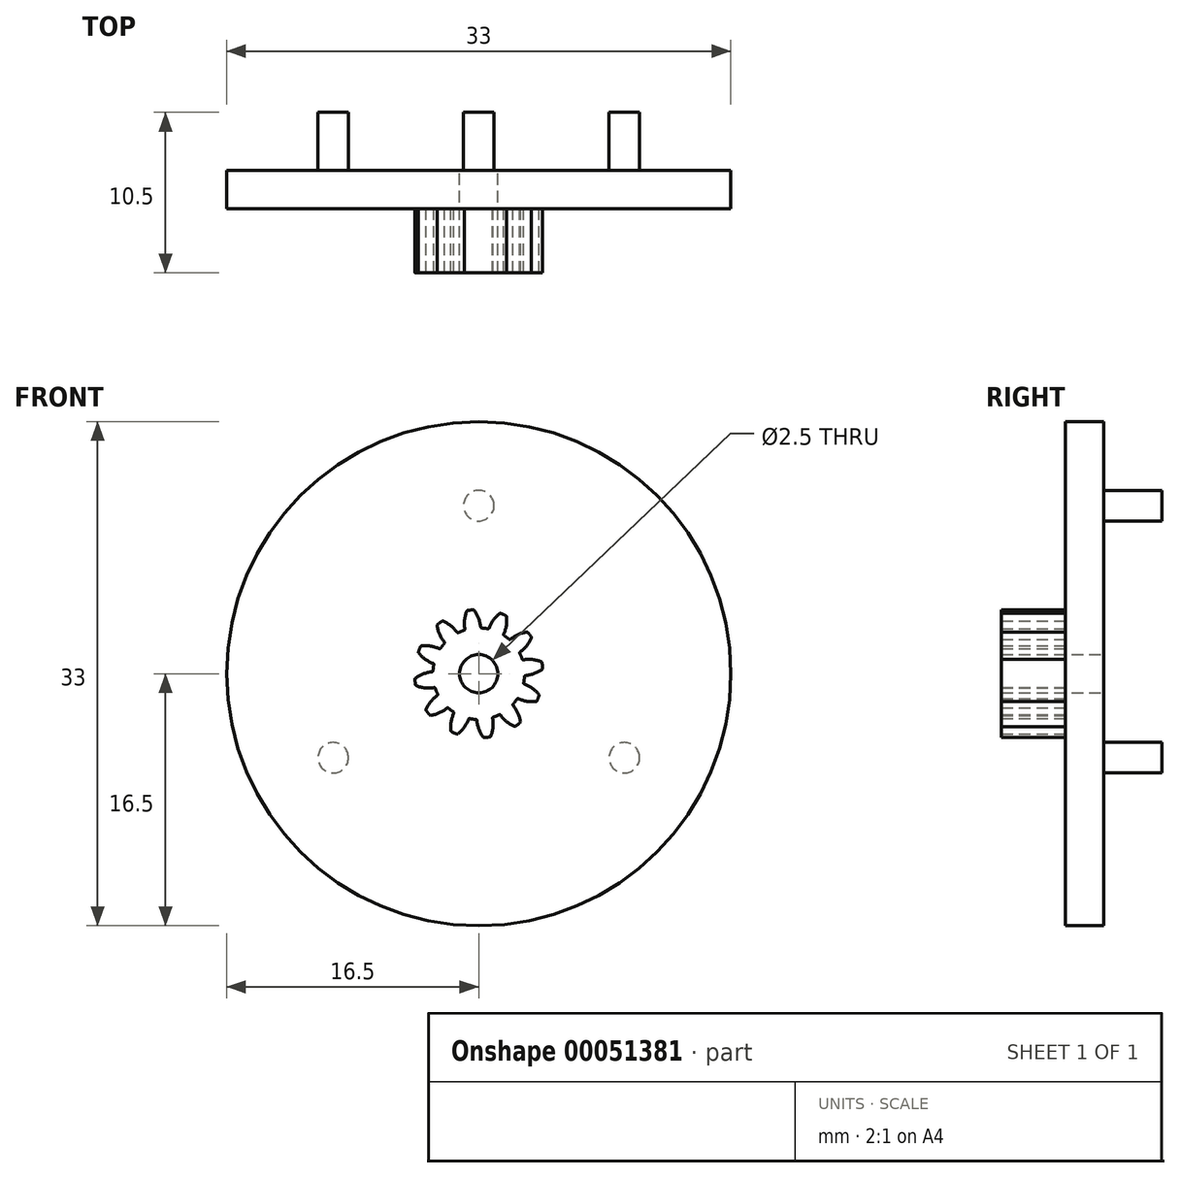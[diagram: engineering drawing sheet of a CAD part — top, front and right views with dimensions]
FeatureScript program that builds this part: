
annotation { "Feature Type Name" : "Feature", "Feature Type Description" : "" }
export const myFeature = defineFeature(function(context is Context, id is Id, definition is map)
    precondition{}
    {
        {
            var Q0;
            Q0=qCreatedBy(makeId("Front.planeOp"),FACE);
            var sketch = newSketch(context, id + "F0", { "sketchPlane" : qUnion([Q0])});
            skCircle(sketch, "E0", {"center": v(0, 0) * mm, "radius": 4.2 * mm, "construction": true});
            skCircle(sketch, "E1", {"center": v(0, 0) * mm, "radius": 3.6 * mm, "construction": true});
            skCircle(sketch, "E2", {"center": v(0, 0) * mm, "radius": 3 * mm, "construction": true});
            skLineSegment(sketch, "E3", {"start": v(0, 0) * mm, "end": v(0, 0.84) * mm, "construction": true});
            skLineSegment(sketch, "E4", {"start": v(0, 3.6) * mm, "end": v(-6.08, 3.6) * mm, "construction": true});
            skLineSegment(sketch, "E5", {"start": v(0, 3.6) * mm, "end": v(-6.1, 1.38) * mm, "construction": true});
            skCircle(sketch, "E6", {"center": v(0, 3.6) * mm, "radius": 2.16 * mm, "construction": true});
            skCircle(sketch, "E7", {"center": v(-2.03, 2.86) * mm, "radius": 2.16 * mm, "construction": true});
            skArc(sketch, "E8", {"start": v(-0.3, 4.16) * mm, "mid": v(-0.01, 3.64) * mm, "end": v(0.12, 3.06) * mm});
            skPoint(sketch, "E9.0.midPoint", {"position": v(-1.28, 0.84) * mm});
            skCircle(sketch, "E10.cCircle", {"center": v(0, 0) * mm, "radius": 0.84 * mm, "construction": true});
            skLineSegment(sketch, "E10.0", {"start": v(0, 0.84) * mm, "end": v(0.1, 0.83) * mm, "construction": true});
            skLineSegment(sketch, "E10.1", {"start": v(0.1, 0.83) * mm, "end": v(0.22, 0.8) * mm, "construction": true});
            skLineSegment(sketch, "E10.2", {"start": v(0.22, 0.8) * mm, "end": v(0.32, 0.77) * mm, "construction": true});
            skLineSegment(sketch, "E10.3", {"start": v(0.32, 0.77) * mm, "end": v(0.42, 0.72) * mm, "construction": true});
            skLineSegment(sketch, "E10.4", {"start": v(0.42, 0.72) * mm, "end": v(0.5, 0.66) * mm, "construction": true});
            skLineSegment(sketch, "E10.5", {"start": v(0.5, 0.66) * mm, "end": v(0.6, 0.6) * mm, "construction": true});
            skLineSegment(sketch, "E10.6", {"start": v(0.6, 0.6) * mm, "end": v(0.66, 0.5) * mm, "construction": true});
            skLineSegment(sketch, "E10.7", {"start": v(0.66, 0.5) * mm, "end": v(0.72, 0.42) * mm, "construction": true});
            skLineSegment(sketch, "E10.8", {"start": v(0.72, 0.42) * mm, "end": v(0.77, 0.32) * mm, "construction": true});
            skLineSegment(sketch, "E10.9", {"start": v(0.77, 0.32) * mm, "end": v(0.8, 0.22) * mm, "construction": true});
            skLineSegment(sketch, "E10.10", {"start": v(0.8, 0.22) * mm, "end": v(0.83, 0.1) * mm, "construction": true});
            skLineSegment(sketch, "E10.11", {"start": v(0.83, 0.1) * mm, "end": v(0.84, 0) * mm, "construction": true});
            skLineSegment(sketch, "E10.12", {"start": v(0.84, 0) * mm, "end": v(0.83, -0.1) * mm, "construction": true});
            skLineSegment(sketch, "E10.13", {"start": v(0.83, -0.1) * mm, "end": v(0.8, -0.22) * mm, "construction": true});
            skLineSegment(sketch, "E10.14", {"start": v(0.8, -0.22) * mm, "end": v(0.77, -0.32) * mm, "construction": true});
            skLineSegment(sketch, "E10.15", {"start": v(0.77, -0.32) * mm, "end": v(0.72, -0.42) * mm, "construction": true});
            skLineSegment(sketch, "E10.16", {"start": v(0.72, -0.42) * mm, "end": v(0.66, -0.5) * mm, "construction": true});
            skLineSegment(sketch, "E10.17", {"start": v(0.66, -0.5) * mm, "end": v(0.6, -0.6) * mm, "construction": true});
            skLineSegment(sketch, "E10.18", {"start": v(0.6, -0.6) * mm, "end": v(0.5, -0.66) * mm, "construction": true});
            skLineSegment(sketch, "E10.19", {"start": v(0.5, -0.66) * mm, "end": v(0.42, -0.72) * mm, "construction": true});
            skLineSegment(sketch, "E10.20", {"start": v(0.42, -0.72) * mm, "end": v(0.32, -0.77) * mm, "construction": true});
            skLineSegment(sketch, "E10.21", {"start": v(0.32, -0.77) * mm, "end": v(0.22, -0.8) * mm, "construction": true});
            skLineSegment(sketch, "E10.22", {"start": v(0.22, -0.8) * mm, "end": v(0.1, -0.83) * mm, "construction": true});
            skLineSegment(sketch, "E10.23", {"start": v(0.1, -0.83) * mm, "end": v(0, -0.84) * mm, "construction": true});
            skLineSegment(sketch, "E10.24", {"start": v(0, -0.84) * mm, "end": v(-0.1, -0.83) * mm, "construction": true});
            skLineSegment(sketch, "E10.25", {"start": v(-0.1, -0.83) * mm, "end": v(-0.22, -0.8) * mm, "construction": true});
            skLineSegment(sketch, "E10.26", {"start": v(-0.22, -0.8) * mm, "end": v(-0.32, -0.77) * mm, "construction": true});
            skLineSegment(sketch, "E10.27", {"start": v(-0.32, -0.77) * mm, "end": v(-0.42, -0.72) * mm, "construction": true});
            skLineSegment(sketch, "E10.28", {"start": v(-0.42, -0.72) * mm, "end": v(-0.5, -0.66) * mm, "construction": true});
            skLineSegment(sketch, "E10.29", {"start": v(-0.5, -0.66) * mm, "end": v(-0.6, -0.6) * mm, "construction": true});
            skLineSegment(sketch, "E10.30", {"start": v(-0.6, -0.6) * mm, "end": v(-0.66, -0.5) * mm, "construction": true});
            skLineSegment(sketch, "E10.31", {"start": v(-0.66, -0.5) * mm, "end": v(-0.72, -0.42) * mm, "construction": true});
            skLineSegment(sketch, "E10.32", {"start": v(-0.72, -0.42) * mm, "end": v(-0.77, -0.32) * mm, "construction": true});
            skLineSegment(sketch, "E10.33", {"start": v(-0.77, -0.32) * mm, "end": v(-0.8, -0.22) * mm, "construction": true});
            skLineSegment(sketch, "E10.34", {"start": v(-0.8, -0.22) * mm, "end": v(-0.83, -0.1) * mm, "construction": true});
            skLineSegment(sketch, "E10.35", {"start": v(-0.83, -0.1) * mm, "end": v(-0.84, 0) * mm, "construction": true});
            skLineSegment(sketch, "E10.36", {"start": v(-0.84, 0) * mm, "end": v(-0.83, 0.1) * mm, "construction": true});
            skLineSegment(sketch, "E10.37", {"start": v(-0.83, 0.1) * mm, "end": v(-0.8, 0.22) * mm, "construction": true});
            skLineSegment(sketch, "E10.38", {"start": v(-0.8, 0.22) * mm, "end": v(-0.77, 0.32) * mm, "construction": true});
            skLineSegment(sketch, "E10.39", {"start": v(-0.77, 0.32) * mm, "end": v(-0.72, 0.42) * mm, "construction": true});
            skLineSegment(sketch, "E10.40", {"start": v(-0.72, 0.42) * mm, "end": v(-0.66, 0.5) * mm, "construction": true});
            skLineSegment(sketch, "E10.41", {"start": v(-0.66, 0.5) * mm, "end": v(-0.6, 0.6) * mm, "construction": true});
            skLineSegment(sketch, "E10.42", {"start": v(-0.6, 0.6) * mm, "end": v(-0.5, 0.66) * mm, "construction": true});
            skLineSegment(sketch, "E10.43", {"start": v(-0.5, 0.66) * mm, "end": v(-0.42, 0.72) * mm, "construction": true});
            skLineSegment(sketch, "E10.44", {"start": v(-0.42, 0.72) * mm, "end": v(-0.32, 0.77) * mm, "construction": true});
            skLineSegment(sketch, "E10.45", {"start": v(-0.32, 0.77) * mm, "end": v(-0.22, 0.8) * mm, "construction": true});
            skLineSegment(sketch, "E10.46", {"start": v(-0.22, 0.8) * mm, "end": v(-0.1, 0.83) * mm, "construction": true});
            skLineSegment(sketch, "E10.47", {"start": v(-0.1, 0.83) * mm, "end": v(0, 0.84) * mm, "construction": true});
            skLineSegment(sketch, "E11", {"start": v(0, 0) * mm, "end": v(-0.1, 0.83) * mm, "construction": true});
            skArc(sketch, "E12.MirrorCS", {"start": v(-0.79, 4.1) * mm, "mid": v(-0.93, 3.52) * mm, "end": v(-0.9, 2.92) * mm});
            skArc(sketch, "E13", {"start": v(-0.73, 4.14) * mm, "mid": v(-0.55, 4.16) * mm, "end": v(-0.36, 4.18) * mm});
            skArc(sketch, "E14", {"start": v(-0.96, 2.84) * mm, "mid": v(0.4, -2.97) * mm, "end": v(0.19, 3) * mm});
            skPoint(sketch, "E15.visualSharp", {"position": v(-0.9, 2.86) * mm});
            skArc(sketch, "E15.filletArc", {"start": v(-0.96, 2.84) * mm, "mid": v(-0.92, 2.87) * mm, "end": v(-0.9, 2.92) * mm});
            skPoint(sketch, "E16.visualSharp", {"position": v(-0.77, 4.13) * mm});
            skArc(sketch, "E16.filletArc", {"start": v(-0.73, 4.14) * mm, "mid": v(-0.76, 4.12) * mm, "end": v(-0.79, 4.1) * mm});
            skPoint(sketch, "E17.visualSharp", {"position": v(-0.32, 4.19) * mm});
            skArc(sketch, "E17.filletArc", {"start": v(-0.3, 4.16) * mm, "mid": v(-0.33, 4.18) * mm, "end": v(-0.36, 4.18) * mm});
            skArc(sketch, "E18.filletArc", {"start": v(0.12, 3.06) * mm, "mid": v(0.14, 3.01) * mm, "end": v(0.19, 3) * mm});
            skArc(sketch, "E19.1.0", {"start": v(-2.25, 1.98) * mm, "mid": v(-2.23, 2.03) * mm, "end": v(-2.25, 2.08) * mm});
            skArc(sketch, "E19.1.1", {"start": v(-2.73, 3.15) * mm, "mid": v(-2.56, 2.58) * mm, "end": v(-2.25, 2.08) * mm});
            skArc(sketch, "E19.1.2", {"start": v(-2.7, 3.22) * mm, "mid": v(-2.72, 3.19) * mm, "end": v(-2.73, 3.15) * mm});
            skArc(sketch, "E19.1.3", {"start": v(-2.7, 3.22) * mm, "mid": v(-2.56, 3.33) * mm, "end": v(-2.4, 3.44) * mm});
            skArc(sketch, "E19.1.4", {"start": v(-2.34, 3.45) * mm, "mid": v(-2.37, 3.45) * mm, "end": v(-2.4, 3.44) * mm});
            skArc(sketch, "E19.1.5", {"start": v(-2.34, 3.45) * mm, "mid": v(-1.83, 3.14) * mm, "end": v(-1.42, 2.71) * mm});
            skArc(sketch, "E19.1.6", {"start": v(-1.42, 2.71) * mm, "mid": v(-1.38, 2.68) * mm, "end": v(-1.33, 2.69) * mm});
            skArc(sketch, "E19.2.0", {"start": v(-2.94, 0.6) * mm, "mid": v(-2.95, 0.64) * mm, "end": v(-2.99, 0.67) * mm});
            skArc(sketch, "E19.2.1", {"start": v(-3.94, 1.37) * mm, "mid": v(-3.5, 0.95) * mm, "end": v(-2.99, 0.67) * mm});
            skArc(sketch, "E19.2.2", {"start": v(-3.95, 1.43) * mm, "mid": v(-3.95, 1.4) * mm, "end": v(-3.94, 1.37) * mm});
            skArc(sketch, "E19.2.3", {"start": v(-3.95, 1.43) * mm, "mid": v(-3.88, 1.6) * mm, "end": v(-3.8, 1.78) * mm});
            skArc(sketch, "E19.2.4", {"start": v(-3.75, 1.82) * mm, "mid": v(-3.78, 1.8) * mm, "end": v(-3.8, 1.78) * mm});
            skArc(sketch, "E19.2.5", {"start": v(-3.75, 1.82) * mm, "mid": v(-3.16, 1.8) * mm, "end": v(-2.59, 1.63) * mm});
            skArc(sketch, "E19.2.6", {"start": v(-2.59, 1.63) * mm, "mid": v(-2.54, 1.63) * mm, "end": v(-2.5, 1.66) * mm});
            skArc(sketch, "E19.3.0", {"start": v(-2.84, -0.96) * mm, "mid": v(-2.87, -0.92) * mm, "end": v(-2.92, -0.9) * mm});
            skArc(sketch, "E19.3.1", {"start": v(-4.1, -0.79) * mm, "mid": v(-3.52, -0.93) * mm, "end": v(-2.92, -0.9) * mm});
            skArc(sketch, "E19.3.2", {"start": v(-4.14, -0.73) * mm, "mid": v(-4.12, -0.76) * mm, "end": v(-4.1, -0.79) * mm});
            skArc(sketch, "E19.3.3", {"start": v(-4.14, -0.73) * mm, "mid": v(-4.16, -0.55) * mm, "end": v(-4.18, -0.36) * mm});
            skArc(sketch, "E19.3.4", {"start": v(-4.16, -0.3) * mm, "mid": v(-4.18, -0.33) * mm, "end": v(-4.18, -0.36) * mm});
            skArc(sketch, "E19.3.5", {"start": v(-4.16, -0.3) * mm, "mid": v(-3.64, -0.01) * mm, "end": v(-3.06, 0.12) * mm});
            skArc(sketch, "E19.3.6", {"start": v(-3.06, 0.12) * mm, "mid": v(-3.01, 0.14) * mm, "end": v(-3, 0.19) * mm});
            skArc(sketch, "E19.4.0", {"start": v(-1.98, -2.25) * mm, "mid": v(-2.03, -2.23) * mm, "end": v(-2.08, -2.25) * mm});
            skArc(sketch, "E19.4.1", {"start": v(-3.15, -2.73) * mm, "mid": v(-2.58, -2.56) * mm, "end": v(-2.08, -2.25) * mm});
            skArc(sketch, "E19.4.2", {"start": v(-3.22, -2.7) * mm, "mid": v(-3.19, -2.72) * mm, "end": v(-3.15, -2.73) * mm});
            skArc(sketch, "E19.4.3", {"start": v(-3.22, -2.7) * mm, "mid": v(-3.33, -2.56) * mm, "end": v(-3.44, -2.4) * mm});
            skArc(sketch, "E19.4.4", {"start": v(-3.45, -2.34) * mm, "mid": v(-3.45, -2.37) * mm, "end": v(-3.44, -2.4) * mm});
            skArc(sketch, "E19.4.5", {"start": v(-3.45, -2.34) * mm, "mid": v(-3.14, -1.83) * mm, "end": v(-2.71, -1.42) * mm});
            skArc(sketch, "E19.4.6", {"start": v(-2.71, -1.42) * mm, "mid": v(-2.68, -1.38) * mm, "end": v(-2.69, -1.33) * mm});
            skArc(sketch, "E19.5.0", {"start": v(-0.6, -2.94) * mm, "mid": v(-0.64, -2.95) * mm, "end": v(-0.67, -2.99) * mm});
            skArc(sketch, "E19.5.1", {"start": v(-1.37, -3.94) * mm, "mid": v(-0.95, -3.5) * mm, "end": v(-0.67, -2.99) * mm});
            skArc(sketch, "E19.5.2", {"start": v(-1.43, -3.95) * mm, "mid": v(-1.4, -3.95) * mm, "end": v(-1.37, -3.94) * mm});
            skArc(sketch, "E19.5.3", {"start": v(-1.43, -3.95) * mm, "mid": v(-1.6, -3.88) * mm, "end": v(-1.78, -3.8) * mm});
            skArc(sketch, "E19.5.4", {"start": v(-1.82, -3.75) * mm, "mid": v(-1.8, -3.78) * mm, "end": v(-1.78, -3.8) * mm});
            skArc(sketch, "E19.5.5", {"start": v(-1.82, -3.75) * mm, "mid": v(-1.8, -3.16) * mm, "end": v(-1.63, -2.59) * mm});
            skArc(sketch, "E19.5.6", {"start": v(-1.63, -2.59) * mm, "mid": v(-1.63, -2.54) * mm, "end": v(-1.66, -2.5) * mm});
            skArc(sketch, "E19.6.0", {"start": v(0.96, -2.84) * mm, "mid": v(0.92, -2.87) * mm, "end": v(0.9, -2.92) * mm});
            skArc(sketch, "E19.6.1", {"start": v(0.79, -4.1) * mm, "mid": v(0.93, -3.52) * mm, "end": v(0.9, -2.92) * mm});
            skArc(sketch, "E19.6.2", {"start": v(0.73, -4.14) * mm, "mid": v(0.76, -4.12) * mm, "end": v(0.79, -4.1) * mm});
            skArc(sketch, "E19.6.3", {"start": v(0.73, -4.14) * mm, "mid": v(0.55, -4.16) * mm, "end": v(0.36, -4.18) * mm});
            skArc(sketch, "E19.6.4", {"start": v(0.3, -4.16) * mm, "mid": v(0.33, -4.18) * mm, "end": v(0.36, -4.18) * mm});
            skArc(sketch, "E19.6.5", {"start": v(0.3, -4.16) * mm, "mid": v(0.01, -3.64) * mm, "end": v(-0.12, -3.06) * mm});
            skArc(sketch, "E19.6.6", {"start": v(-0.12, -3.06) * mm, "mid": v(-0.14, -3.01) * mm, "end": v(-0.19, -3) * mm});
            skArc(sketch, "E19.7.0", {"start": v(2.25, -1.98) * mm, "mid": v(2.23, -2.03) * mm, "end": v(2.25, -2.08) * mm});
            skArc(sketch, "E19.7.1", {"start": v(2.73, -3.15) * mm, "mid": v(2.56, -2.58) * mm, "end": v(2.25, -2.08) * mm});
            skArc(sketch, "E19.7.2", {"start": v(2.7, -3.22) * mm, "mid": v(2.72, -3.19) * mm, "end": v(2.73, -3.15) * mm});
            skArc(sketch, "E19.7.3", {"start": v(2.7, -3.22) * mm, "mid": v(2.56, -3.33) * mm, "end": v(2.4, -3.44) * mm});
            skArc(sketch, "E19.7.4", {"start": v(2.34, -3.45) * mm, "mid": v(2.37, -3.45) * mm, "end": v(2.4, -3.44) * mm});
            skArc(sketch, "E19.7.5", {"start": v(2.34, -3.45) * mm, "mid": v(1.83, -3.14) * mm, "end": v(1.42, -2.71) * mm});
            skArc(sketch, "E19.7.6", {"start": v(1.42, -2.71) * mm, "mid": v(1.38, -2.68) * mm, "end": v(1.33, -2.69) * mm});
            skArc(sketch, "E19.8.0", {"start": v(2.94, -0.6) * mm, "mid": v(2.95, -0.64) * mm, "end": v(2.99, -0.67) * mm});
            skArc(sketch, "E19.8.1", {"start": v(3.94, -1.37) * mm, "mid": v(3.5, -0.95) * mm, "end": v(2.99, -0.67) * mm});
            skArc(sketch, "E19.8.2", {"start": v(3.95, -1.43) * mm, "mid": v(3.95, -1.4) * mm, "end": v(3.94, -1.37) * mm});
            skArc(sketch, "E19.8.3", {"start": v(3.95, -1.43) * mm, "mid": v(3.88, -1.6) * mm, "end": v(3.8, -1.78) * mm});
            skArc(sketch, "E19.8.4", {"start": v(3.75, -1.82) * mm, "mid": v(3.78, -1.8) * mm, "end": v(3.8, -1.78) * mm});
            skArc(sketch, "E19.8.5", {"start": v(3.75, -1.82) * mm, "mid": v(3.16, -1.8) * mm, "end": v(2.59, -1.63) * mm});
            skArc(sketch, "E19.8.6", {"start": v(2.59, -1.63) * mm, "mid": v(2.54, -1.63) * mm, "end": v(2.5, -1.66) * mm});
            skArc(sketch, "E19.9.0", {"start": v(2.84, 0.96) * mm, "mid": v(2.87, 0.92) * mm, "end": v(2.92, 0.9) * mm});
            skArc(sketch, "E19.9.1", {"start": v(4.1, 0.79) * mm, "mid": v(3.52, 0.93) * mm, "end": v(2.92, 0.9) * mm});
            skArc(sketch, "E19.9.2", {"start": v(4.14, 0.73) * mm, "mid": v(4.12, 0.76) * mm, "end": v(4.1, 0.79) * mm});
            skArc(sketch, "E19.9.3", {"start": v(4.14, 0.73) * mm, "mid": v(4.16, 0.55) * mm, "end": v(4.18, 0.36) * mm});
            skArc(sketch, "E19.9.4", {"start": v(4.16, 0.3) * mm, "mid": v(4.18, 0.33) * mm, "end": v(4.18, 0.36) * mm});
            skArc(sketch, "E19.9.5", {"start": v(4.16, 0.3) * mm, "mid": v(3.64, 0.01) * mm, "end": v(3.06, -0.12) * mm});
            skArc(sketch, "E19.9.6", {"start": v(3.06, -0.12) * mm, "mid": v(3.01, -0.14) * mm, "end": v(3, -0.19) * mm});
            skArc(sketch, "E19.10.0", {"start": v(1.98, 2.25) * mm, "mid": v(2.03, 2.23) * mm, "end": v(2.08, 2.25) * mm});
            skArc(sketch, "E19.10.1", {"start": v(3.15, 2.73) * mm, "mid": v(2.58, 2.56) * mm, "end": v(2.08, 2.25) * mm});
            skArc(sketch, "E19.10.2", {"start": v(3.22, 2.7) * mm, "mid": v(3.19, 2.72) * mm, "end": v(3.15, 2.73) * mm});
            skArc(sketch, "E19.10.3", {"start": v(3.22, 2.7) * mm, "mid": v(3.33, 2.56) * mm, "end": v(3.44, 2.4) * mm});
            skArc(sketch, "E19.10.4", {"start": v(3.45, 2.34) * mm, "mid": v(3.45, 2.37) * mm, "end": v(3.44, 2.4) * mm});
            skArc(sketch, "E19.10.5", {"start": v(3.45, 2.34) * mm, "mid": v(3.14, 1.83) * mm, "end": v(2.71, 1.42) * mm});
            skArc(sketch, "E19.10.6", {"start": v(2.71, 1.42) * mm, "mid": v(2.68, 1.38) * mm, "end": v(2.69, 1.33) * mm});
            skArc(sketch, "E19.11.0", {"start": v(0.6, 2.94) * mm, "mid": v(0.64, 2.95) * mm, "end": v(0.67, 2.99) * mm});
            skArc(sketch, "E19.11.1", {"start": v(1.37, 3.94) * mm, "mid": v(0.95, 3.5) * mm, "end": v(0.67, 2.99) * mm});
            skArc(sketch, "E19.11.2", {"start": v(1.43, 3.95) * mm, "mid": v(1.4, 3.95) * mm, "end": v(1.37, 3.94) * mm});
            skArc(sketch, "E19.11.3", {"start": v(1.43, 3.95) * mm, "mid": v(1.6, 3.88) * mm, "end": v(1.78, 3.8) * mm});
            skArc(sketch, "E19.11.4", {"start": v(1.82, 3.75) * mm, "mid": v(1.8, 3.78) * mm, "end": v(1.78, 3.8) * mm});
            skArc(sketch, "E19.11.5", {"start": v(1.82, 3.75) * mm, "mid": v(1.8, 3.16) * mm, "end": v(1.63, 2.59) * mm});
            skArc(sketch, "E19.11.6", {"start": v(1.63, 2.59) * mm, "mid": v(1.63, 2.54) * mm, "end": v(1.66, 2.5) * mm});
            skSolve(sketch);
        }
        {
            var Q0;
            Q0 = qSketchRegion(id + "F0", true);
            extrude(context, id + "F1", {"entities" : qUnion([Q0]), "depth" : 4.2 * mm});
        }
        {
            var Q0;
            Q0=makeQuery(id+"F1.opExtrude","CAP_FACE",FACE,{"disambiguationData":[OSD([sQuery(id+"F0.wireOp",EDGE,"E8"),sQuery(id+"F0.wireOp",EDGE,"E12.MirrorCS"),sQuery(id+"F0.wireOp",EDGE,"E13"),sQuery(id+"F0.wireOp",EDGE,"E14"),sQuery(id+"F0.wireOp",EDGE,"E15.filletArc"),sQuery(id+"F0.wireOp",EDGE,"E16.filletArc"),sQuery(id+"F0.wireOp",EDGE,"E17.filletArc"),sQuery(id+"F0.wireOp",EDGE,"E18.filletArc"),sQuery(id+"F0.wireOp",EDGE,"E19.1.0"),sQuery(id+"F0.wireOp",EDGE,"E19.1.1"),sQuery(id+"F0.wireOp",EDGE,"E19.1.2"),sQuery(id+"F0.wireOp",EDGE,"E19.1.3"),sQuery(id+"F0.wireOp",EDGE,"E19.1.4"),sQuery(id+"F0.wireOp",EDGE,"E19.1.5"),sQuery(id+"F0.wireOp",EDGE,"E19.1.6"),sQuery(id+"F0.wireOp",EDGE,"E19.2.0"),sQuery(id+"F0.wireOp",EDGE,"E19.2.1"),sQuery(id+"F0.wireOp",EDGE,"E19.2.2"),sQuery(id+"F0.wireOp",EDGE,"E19.2.3"),sQuery(id+"F0.wireOp",EDGE,"E19.2.4"),sQuery(id+"F0.wireOp",EDGE,"E19.2.5"),sQuery(id+"F0.wireOp",EDGE,"E19.2.6"),sQuery(id+"F0.wireOp",EDGE,"E19.3.0"),sQuery(id+"F0.wireOp",EDGE,"E19.3.1"),sQuery(id+"F0.wireOp",EDGE,"E19.3.2"),sQuery(id+"F0.wireOp",EDGE,"E19.3.3"),sQuery(id+"F0.wireOp",EDGE,"E19.3.4"),sQuery(id+"F0.wireOp",EDGE,"E19.3.5"),sQuery(id+"F0.wireOp",EDGE,"E19.3.6"),sQuery(id+"F0.wireOp",EDGE,"E19.4.0"),sQuery(id+"F0.wireOp",EDGE,"E19.4.1"),sQuery(id+"F0.wireOp",EDGE,"E19.4.2"),sQuery(id+"F0.wireOp",EDGE,"E19.4.3"),sQuery(id+"F0.wireOp",EDGE,"E19.4.4"),sQuery(id+"F0.wireOp",EDGE,"E19.4.5"),sQuery(id+"F0.wireOp",EDGE,"E19.4.6"),sQuery(id+"F0.wireOp",EDGE,"E19.5.0"),sQuery(id+"F0.wireOp",EDGE,"E19.5.1"),sQuery(id+"F0.wireOp",EDGE,"E19.5.2"),sQuery(id+"F0.wireOp",EDGE,"E19.5.3"),sQuery(id+"F0.wireOp",EDGE,"E19.5.4"),sQuery(id+"F0.wireOp",EDGE,"E19.5.5"),sQuery(id+"F0.wireOp",EDGE,"E19.5.6"),sQuery(id+"F0.wireOp",EDGE,"E19.6.0"),sQuery(id+"F0.wireOp",EDGE,"E19.6.1"),sQuery(id+"F0.wireOp",EDGE,"E19.6.2"),sQuery(id+"F0.wireOp",EDGE,"E19.6.3"),sQuery(id+"F0.wireOp",EDGE,"E19.6.4"),sQuery(id+"F0.wireOp",EDGE,"E19.6.5"),sQuery(id+"F0.wireOp",EDGE,"E19.6.6"),sQuery(id+"F0.wireOp",EDGE,"E19.7.0"),sQuery(id+"F0.wireOp",EDGE,"E19.7.1"),sQuery(id+"F0.wireOp",EDGE,"E19.7.2"),sQuery(id+"F0.wireOp",EDGE,"E19.7.3"),sQuery(id+"F0.wireOp",EDGE,"E19.7.4"),sQuery(id+"F0.wireOp",EDGE,"E19.7.5"),sQuery(id+"F0.wireOp",EDGE,"E19.7.6"),sQuery(id+"F0.wireOp",EDGE,"E19.8.0"),sQuery(id+"F0.wireOp",EDGE,"E19.8.1"),sQuery(id+"F0.wireOp",EDGE,"E19.8.2"),sQuery(id+"F0.wireOp",EDGE,"E19.8.3"),sQuery(id+"F0.wireOp",EDGE,"E19.8.4"),sQuery(id+"F0.wireOp",EDGE,"E19.8.5"),sQuery(id+"F0.wireOp",EDGE,"E19.8.6"),sQuery(id+"F0.wireOp",EDGE,"E19.9.0"),sQuery(id+"F0.wireOp",EDGE,"E19.9.1"),sQuery(id+"F0.wireOp",EDGE,"E19.9.2"),sQuery(id+"F0.wireOp",EDGE,"E19.9.3"),sQuery(id+"F0.wireOp",EDGE,"E19.9.4"),sQuery(id+"F0.wireOp",EDGE,"E19.9.5"),sQuery(id+"F0.wireOp",EDGE,"E19.9.6"),sQuery(id+"F0.wireOp",EDGE,"E19.10.0"),sQuery(id+"F0.wireOp",EDGE,"E19.10.1"),sQuery(id+"F0.wireOp",EDGE,"E19.10.2"),sQuery(id+"F0.wireOp",EDGE,"E19.10.3"),sQuery(id+"F0.wireOp",EDGE,"E19.10.4"),sQuery(id+"F0.wireOp",EDGE,"E19.10.5"),sQuery(id+"F0.wireOp",EDGE,"E19.10.6"),sQuery(id+"F0.wireOp",EDGE,"E19.11.0"),sQuery(id+"F0.wireOp",EDGE,"E19.11.1"),sQuery(id+"F0.wireOp",EDGE,"E19.11.2"),sQuery(id+"F0.wireOp",EDGE,"E19.11.3"),sQuery(id+"F0.wireOp",EDGE,"E19.11.4"),sQuery(id+"F0.wireOp",EDGE,"E19.11.5"),sQuery(id+"F0.wireOp",EDGE,"E19.11.6")])],"isStart":true});
            var sketch = newSketch(context, id + "F2", { "sketchPlane" : qUnion([Q0])});
            skCircle(sketch, "E20", {"center": v(0, 0) * mm, "radius": 16.5 * mm});
            skSolve(sketch);
        }
        {
            var Q0;
            Q0 = qSketchRegion(id + "F2", true);
            extrude(context, id + "F3", {"entities" : qUnion([Q0]), "operationType" : NewBodyOperationType.ADD, "depth" : 2.5 * mm});
        }
        {
            var Q0;
            Q0=makeQuery(id+"F3.opExtrude","CAP_FACE",FACE,{"disambiguationData":[OSD([sQuery(id+"F2.wireOp",EDGE,"E20")])],"isStart":false});
            var sketch = newSketch(context, id + "F4", { "sketchPlane" : qUnion([Q0])});
            skLineSegment(sketch, "E21", {"start": v(0, 0) * mm, "end": v(0, 5.49) * mm, "construction": true});
            skCircle(sketch, "E22", {"center": v(0, 11) * mm, "radius": 1 * mm});
            skCircle(sketch, "E23.1.0", {"center": v(-9.53, -5.5) * mm, "radius": 1 * mm});
            skCircle(sketch, "E23.2.0", {"center": v(9.53, -5.5) * mm, "radius": 1 * mm});
            skPoint(sketch, "E23.center", {"position": v(0, 0) * mm});
            skSolve(sketch);
        }
        {
            var Q0;
            Q0 = qSketchRegion(id + "F4", true);
            extrude(context, id + "F5", {"entities" : qUnion([Q0]), "operationType" : NewBodyOperationType.ADD, "depth" : 3.8 * mm});
        }
        {
            var Q0;
            Q0=makeQuery(id+"F1.opExtrude","CAP_FACE",FACE,{"disambiguationData":[OSD([sQuery(id+"F0.wireOp",EDGE,"E8"),sQuery(id+"F0.wireOp",EDGE,"E12.MirrorCS"),sQuery(id+"F0.wireOp",EDGE,"E13"),sQuery(id+"F0.wireOp",EDGE,"E14"),sQuery(id+"F0.wireOp",EDGE,"E15.filletArc"),sQuery(id+"F0.wireOp",EDGE,"E16.filletArc"),sQuery(id+"F0.wireOp",EDGE,"E17.filletArc"),sQuery(id+"F0.wireOp",EDGE,"E18.filletArc"),sQuery(id+"F0.wireOp",EDGE,"E19.1.0"),sQuery(id+"F0.wireOp",EDGE,"E19.1.1"),sQuery(id+"F0.wireOp",EDGE,"E19.1.2"),sQuery(id+"F0.wireOp",EDGE,"E19.1.3"),sQuery(id+"F0.wireOp",EDGE,"E19.1.4"),sQuery(id+"F0.wireOp",EDGE,"E19.1.5"),sQuery(id+"F0.wireOp",EDGE,"E19.1.6"),sQuery(id+"F0.wireOp",EDGE,"E19.2.0"),sQuery(id+"F0.wireOp",EDGE,"E19.2.1"),sQuery(id+"F0.wireOp",EDGE,"E19.2.2"),sQuery(id+"F0.wireOp",EDGE,"E19.2.3"),sQuery(id+"F0.wireOp",EDGE,"E19.2.4"),sQuery(id+"F0.wireOp",EDGE,"E19.2.5"),sQuery(id+"F0.wireOp",EDGE,"E19.2.6"),sQuery(id+"F0.wireOp",EDGE,"E19.3.0"),sQuery(id+"F0.wireOp",EDGE,"E19.3.1"),sQuery(id+"F0.wireOp",EDGE,"E19.3.2"),sQuery(id+"F0.wireOp",EDGE,"E19.3.3"),sQuery(id+"F0.wireOp",EDGE,"E19.3.4"),sQuery(id+"F0.wireOp",EDGE,"E19.3.5"),sQuery(id+"F0.wireOp",EDGE,"E19.3.6"),sQuery(id+"F0.wireOp",EDGE,"E19.4.0"),sQuery(id+"F0.wireOp",EDGE,"E19.4.1"),sQuery(id+"F0.wireOp",EDGE,"E19.4.2"),sQuery(id+"F0.wireOp",EDGE,"E19.4.3"),sQuery(id+"F0.wireOp",EDGE,"E19.4.4"),sQuery(id+"F0.wireOp",EDGE,"E19.4.5"),sQuery(id+"F0.wireOp",EDGE,"E19.4.6"),sQuery(id+"F0.wireOp",EDGE,"E19.5.0"),sQuery(id+"F0.wireOp",EDGE,"E19.5.1"),sQuery(id+"F0.wireOp",EDGE,"E19.5.2"),sQuery(id+"F0.wireOp",EDGE,"E19.5.3"),sQuery(id+"F0.wireOp",EDGE,"E19.5.4"),sQuery(id+"F0.wireOp",EDGE,"E19.5.5"),sQuery(id+"F0.wireOp",EDGE,"E19.5.6"),sQuery(id+"F0.wireOp",EDGE,"E19.6.0"),sQuery(id+"F0.wireOp",EDGE,"E19.6.1"),sQuery(id+"F0.wireOp",EDGE,"E19.6.2"),sQuery(id+"F0.wireOp",EDGE,"E19.6.3"),sQuery(id+"F0.wireOp",EDGE,"E19.6.4"),sQuery(id+"F0.wireOp",EDGE,"E19.6.5"),sQuery(id+"F0.wireOp",EDGE,"E19.6.6"),sQuery(id+"F0.wireOp",EDGE,"E19.7.0"),sQuery(id+"F0.wireOp",EDGE,"E19.7.1"),sQuery(id+"F0.wireOp",EDGE,"E19.7.2"),sQuery(id+"F0.wireOp",EDGE,"E19.7.3"),sQuery(id+"F0.wireOp",EDGE,"E19.7.4"),sQuery(id+"F0.wireOp",EDGE,"E19.7.5"),sQuery(id+"F0.wireOp",EDGE,"E19.7.6"),sQuery(id+"F0.wireOp",EDGE,"E19.8.0"),sQuery(id+"F0.wireOp",EDGE,"E19.8.1"),sQuery(id+"F0.wireOp",EDGE,"E19.8.2"),sQuery(id+"F0.wireOp",EDGE,"E19.8.3"),sQuery(id+"F0.wireOp",EDGE,"E19.8.4"),sQuery(id+"F0.wireOp",EDGE,"E19.8.5"),sQuery(id+"F0.wireOp",EDGE,"E19.8.6"),sQuery(id+"F0.wireOp",EDGE,"E19.9.0"),sQuery(id+"F0.wireOp",EDGE,"E19.9.1"),sQuery(id+"F0.wireOp",EDGE,"E19.9.2"),sQuery(id+"F0.wireOp",EDGE,"E19.9.3"),sQuery(id+"F0.wireOp",EDGE,"E19.9.4"),sQuery(id+"F0.wireOp",EDGE,"E19.9.5"),sQuery(id+"F0.wireOp",EDGE,"E19.9.6"),sQuery(id+"F0.wireOp",EDGE,"E19.10.0"),sQuery(id+"F0.wireOp",EDGE,"E19.10.1"),sQuery(id+"F0.wireOp",EDGE,"E19.10.2"),sQuery(id+"F0.wireOp",EDGE,"E19.10.3"),sQuery(id+"F0.wireOp",EDGE,"E19.10.4"),sQuery(id+"F0.wireOp",EDGE,"E19.10.5"),sQuery(id+"F0.wireOp",EDGE,"E19.10.6"),sQuery(id+"F0.wireOp",EDGE,"E19.11.0"),sQuery(id+"F0.wireOp",EDGE,"E19.11.1"),sQuery(id+"F0.wireOp",EDGE,"E19.11.2"),sQuery(id+"F0.wireOp",EDGE,"E19.11.3"),sQuery(id+"F0.wireOp",EDGE,"E19.11.4"),sQuery(id+"F0.wireOp",EDGE,"E19.11.5"),sQuery(id+"F0.wireOp",EDGE,"E19.11.6")])],"isStart":false});
            var sketch = newSketch(context, id + "F6", { "sketchPlane" : qUnion([Q0])});
            skCircle(sketch, "E24", {"center": v(0, 0) * mm, "radius": 1.25 * mm});
            skSolve(sketch);
        }
        {
            var Q0;
            Q0 = qSketchRegion(id + "F6", true);
            extrude(context, id + "F7", {"entities" : qUnion([Q0]), "operationType" : NewBodyOperationType.REMOVE, "depth" : 25 * mm, "hasSecondDirection" : true, "secondDirectionOppositeDirection" : true, "secondDirectionDepth" : 25 * mm});
        }
    });
